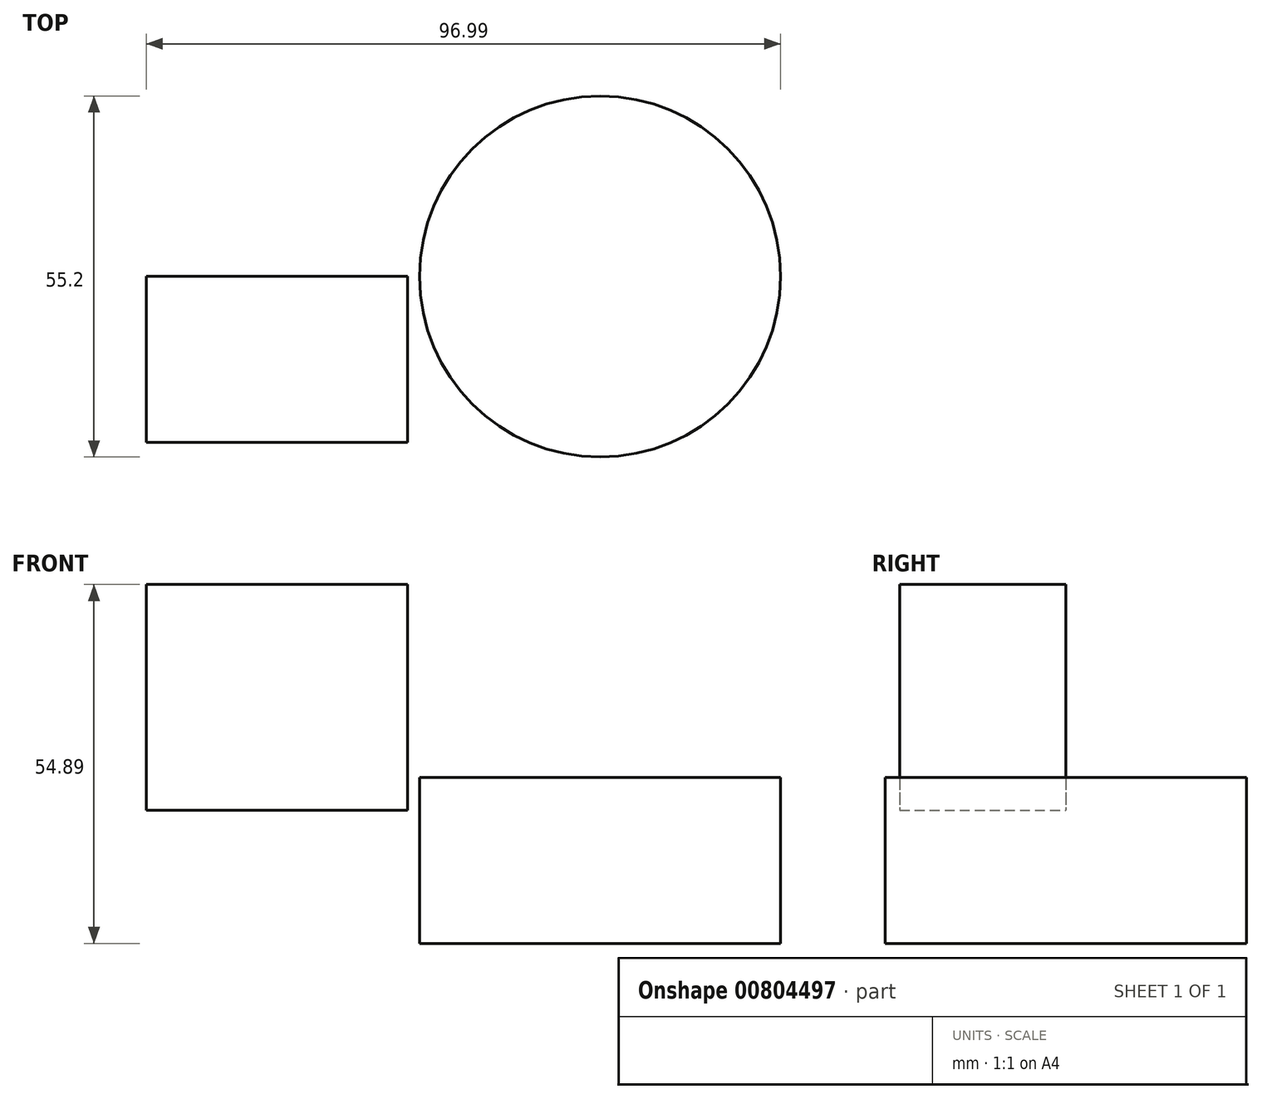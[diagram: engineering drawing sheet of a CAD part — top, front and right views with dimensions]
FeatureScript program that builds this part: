
annotation { "Feature Type Name" : "Feature", "Feature Type Description" : "" }
export const myFeature = defineFeature(function(context is Context, id is Id, definition is map)
    precondition{}
    {
        {
            var Q0;
            Q0=qCreatedBy(makeId("Front.planeOp"),FACE);
            var sketch = newSketch(context, id + "F0", { "sketchPlane" : qUnion([Q0])});
            skLineSegment(sketch, "E0.bottom", {"start": v(-48.52, 54.9) * mm, "end": v(-8.59, 54.9) * mm});
            skLineSegment(sketch, "E0.top", {"start": v(-48.52, 20.4) * mm, "end": v(-8.59, 20.4) * mm});
            skLineSegment(sketch, "E0.left", {"start": v(-48.52, 54.9) * mm, "end": v(-48.52, 20.4) * mm});
            skLineSegment(sketch, "E0.right", {"start": v(-8.59, 54.9) * mm, "end": v(-8.59, 20.4) * mm});
            skSolve(sketch);
        }
        {
            var Q0;
            Q0=makeQuery(id+"F0.imprint","IMPRINT",FACE,{"disambiguationData":[TD([[makeQuery(id+"F0.imprint","IMPRINT",EDGE,{"derivedFrom":sQuery(id+"F0.wireOp",EDGE,"E0.bottom")}),-1.0]])]});
            extrude(context, id + "F1", {"entities" : qUnion([Q0]), "depth" : 25.4 * mm, "offsetDistance" : 25.4 * mm});
        }
        {
            var Q0;
            Q0=qCreatedBy(makeId("Top.planeOp"),FACE);
            var sketch = newSketch(context, id + "F2", { "sketchPlane" : qUnion([Q0])});
            skCircle(sketch, "E1", {"center": v(20.86, 0) * mm, "radius": 27.6 * mm});
            skSolve(sketch);
        }
        {
            var Q0;
            Q0=makeQuery(id+"F2.imprint","IMPRINT",FACE,{"disambiguationData":[TD([[makeQuery(id+"F2.imprint","IMPRINT",EDGE,{"derivedFrom":sQuery(id+"F2.wireOp",EDGE,"E1")}),1.0]])]});
            extrude(context, id + "F3", {"entities" : qUnion([Q0]), "depth" : 25.4 * mm, "offsetDistance" : 25.4 * mm});
        }
    });
